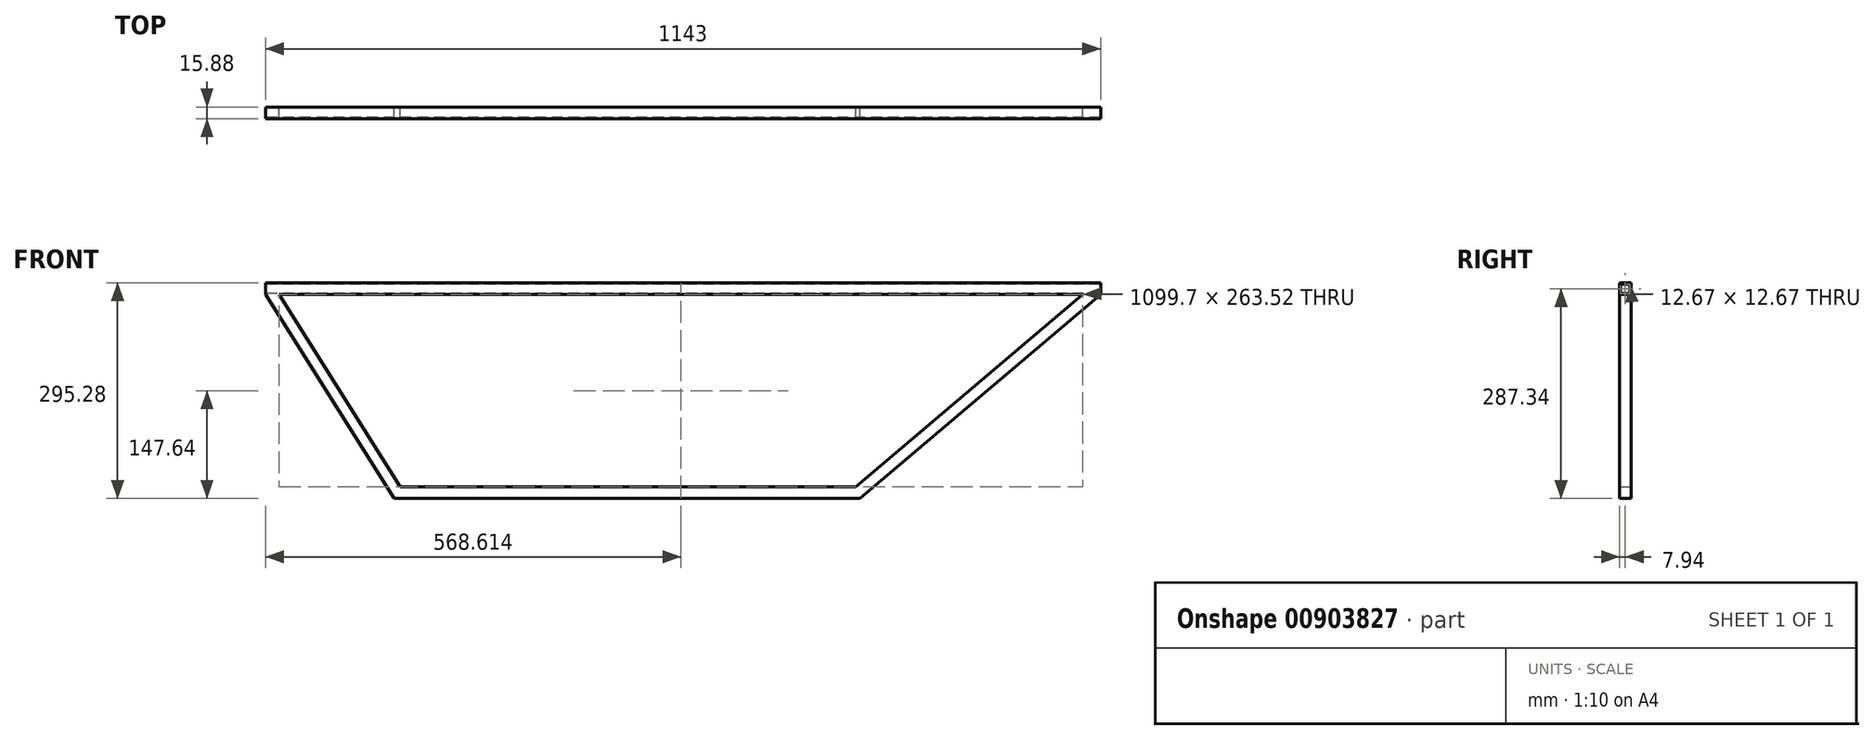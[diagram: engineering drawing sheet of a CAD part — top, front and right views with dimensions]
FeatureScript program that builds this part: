
annotation { "Feature Type Name" : "Feature", "Feature Type Description" : "" }
export const myFeature = defineFeature(function(context is Context, id is Id, definition is map)
    precondition{}
    {
        {
            var Q0;
            Q0=qCreatedBy(makeId("Front.planeOp"),FACE);
            var sketch = newSketch(context, id + "F0", { "sketchPlane" : qUnion([Q0])});
            skLineSegment(sketch, "E0", {"start": v(0, 0) * mm, "end": v(571.5, 0) * mm, "construction": true});
            skLineSegment(sketch, "E1", {"start": v(571.5, 0) * mm, "end": v(571.5, -7.94) * mm, "construction": true});
            skLineSegment(sketch, "E2", {"start": v(0, 0) * mm, "end": v(0, -287.34) * mm, "construction": true});
            skLineSegment(sketch, "E3", {"start": v(571.5, -7.94) * mm, "end": v(242.28, -287.34) * mm});
            skLineSegment(sketch, "E4", {"start": v(0, 0) * mm, "end": v(-571.5, 0) * mm, "construction": true});
            skLineSegment(sketch, "E5", {"start": v(-571.5, 0) * mm, "end": v(-571.5, -7.94) * mm, "construction": true});
            skLineSegment(sketch, "E6", {"start": v(-571.5, -7.94) * mm, "end": v(-395.52, -287.34) * mm});
            skLineSegment(sketch, "E7.0", {"start": v(-558.07, 0.52) * mm, "end": v(-557.74, 0) * mm});
            skLineSegment(sketch, "E8", {"start": v(-552.74, -7.94) * mm, "end": v(546.97, -7.94) * mm});
            skLineSegment(sketch, "E9.0", {"start": v(-571.5, 7.94) * mm, "end": v(571.5, 7.94) * mm});
            skLineSegment(sketch, "E10", {"start": v(-571.5, 7.94) * mm, "end": v(-571.5, -7.94) * mm});
            skLineSegment(sketch, "E11", {"start": v(-395.52, -287.34) * mm, "end": v(242.28, -287.34) * mm});
            skLineSegment(sketch, "E12", {"start": v(242.28, -287.34) * mm, "end": v(242.28, -271.46) * mm, "construction": true});
            skLineSegment(sketch, "E13.0", {"start": v(-386.76, -271.46) * mm, "end": v(236.45, -271.46) * mm});
            skLineSegment(sketch, "E14", {"start": v(571.5, 7.94) * mm, "end": v(571.5, -7.94) * mm});
            skLineSegment(sketch, "E15.trimOffspring", {"start": v(-552.74, -7.94) * mm, "end": v(-386.76, -271.46) * mm});
            skLineSegment(sketch, "E16.trimOffspring", {"start": v(546.97, -7.94) * mm, "end": v(236.45, -271.46) * mm});
            skSolve(sketch);
        }
        {
            var Q0;
            Q0 = qSketchRegion(id + "F0", true);
            extrude(context, id + "F1", {"entities" : qUnion([Q0]), "depth" : 15.88 * mm, "offsetDistance" : 25.4 * mm, "symmetric" : true});
        }
        {
            var Q0;
            Q0=makeQuery(id+"F1.opExtrude","SWEPT_FACE",FACE,{"disambiguationData":[OSD([sQuery(id+"F0.wireOp",EDGE,"E10")])]});
            var sketch = newSketch(context, id + "F2", { "sketchPlane" : qUnion([Q0])});
            skLineSegment(sketch, "E17.bottom", {"start": v(6.34, -6.34) * mm, "end": v(-6.34, -6.34) * mm});
            skLineSegment(sketch, "E17.top", {"start": v(6.34, 6.34) * mm, "end": v(-6.34, 6.34) * mm});
            skLineSegment(sketch, "E17.left", {"start": v(6.34, -6.34) * mm, "end": v(6.34, 6.34) * mm});
            skLineSegment(sketch, "E17.right", {"start": v(-6.34, -6.34) * mm, "end": v(-6.34, 6.34) * mm});
            skPoint(sketch, "E17.middle", {"position": v(0, 0) * mm});
            skSolve(sketch);
        }
        {
            var Q0;
            Q0 = qSketchRegion(id + "F2", true);
            extrude(context, id + "F3", {"entities" : qUnion([Q0]), "operationType" : NewBodyOperationType.REMOVE, "endBound" : BoundingType.THROUGH_ALL, "oppositeDirection" : true, "depth" : 25.4 * mm, "offsetDistance" : 25.4 * mm, "hasSecondDirection" : true, "secondDirectionBound" : BoundingType.THROUGH_ALL, "secondDirectionOppositeDirection" : false, "secondDirectionDepth" : 25.4 * mm});
        }
    });
